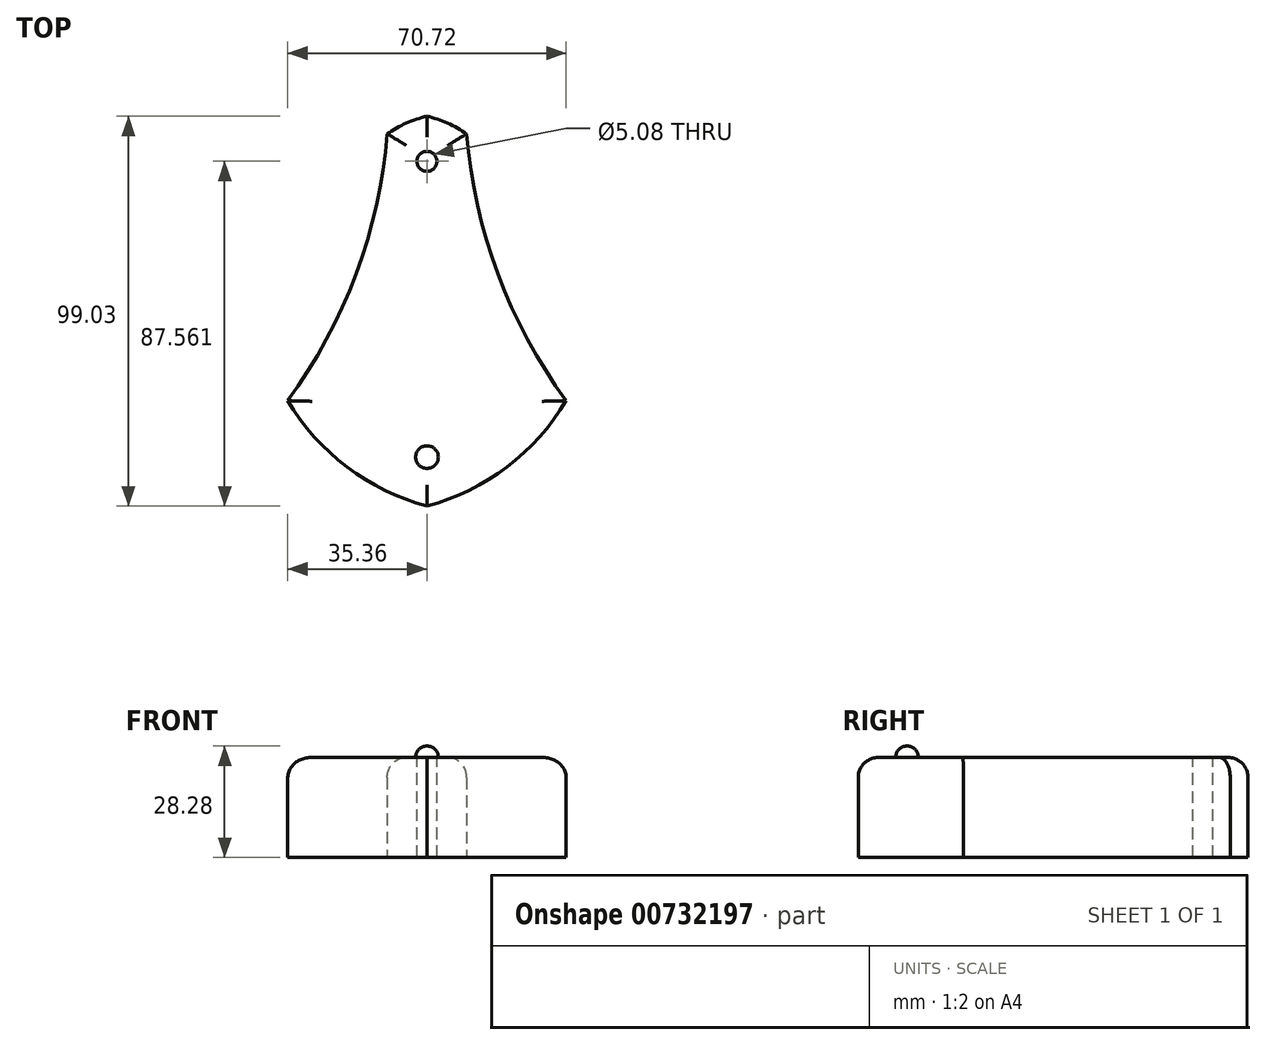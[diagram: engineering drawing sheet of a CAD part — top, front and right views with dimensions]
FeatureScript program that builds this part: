
annotation { "Feature Type Name" : "Feature", "Feature Type Description" : "" }
export const myFeature = defineFeature(function(context is Context, id is Id, definition is map)
    precondition{}
    {
        {
            var Q0;
            Q0=qCreatedBy(makeId("Top.planeOp"),FACE);
            var sketch = newSketch(context, id + "F0", { "sketchPlane" : qUnion([Q0])});
            skArc(sketch, "E0", {"start": v(0, 52.74) * mm, "mid": v(-5.26, 50.96) * mm, "end": v(-10.1, 48.22) * mm});
            skArc(sketch, "E1", {"start": v(-35.36, -19.52) * mm, "mid": v(-18.04, 12.6) * mm, "end": v(-10.1, 48.22) * mm});
            skArc(sketch, "E2", {"start": v(-35.36, -19.52) * mm, "mid": v(-20.32, -36.4) * mm, "end": v(0, -46.29) * mm});
            skArc(sketch, "E3.MirrorCS", {"start": v(35.36, -19.52) * mm, "mid": v(18.04, 12.6) * mm, "end": v(10.1, 48.22) * mm});
            skArc(sketch, "E4.MirrorCS", {"start": v(35.36, -19.52) * mm, "mid": v(20.32, -36.4) * mm, "end": v(0, -46.29) * mm});
            skArc(sketch, "E5.MirrorCS", {"start": v(0, 52.74) * mm, "mid": v(5.26, 50.96) * mm, "end": v(10.1, 48.22) * mm});
            skSolve(sketch);
        }
        {
            var Q0;
            Q0=makeQuery(id+"F0.imprint","IMPRINT",FACE,{"disambiguationData":[TD([[makeQuery(id+"F0.imprint","IMPRINT",EDGE,{"derivedFrom":sQuery(id+"F0.wireOp",EDGE,"E0")}),1.0]])]});
            extrude(context, id + "F1", {"entities" : qUnion([Q0]), "depth" : 25.4 * mm, "offsetDistance" : 25.4 * mm});
        }
        {
            var Q0;
            Q0=makeQuery(id+"F1.opExtrude","CAP_EDGE",EDGE,{"disambiguationData":[OSD([sQuery(id+"F0.wireOp",EDGE,"E2")])],"isStart":false});
            var Q1;
            Q1=makeQuery(id+"F1.opExtrude","CAP_FACE",FACE,{"disambiguationData":[OSD([sQuery(id+"F0.wireOp",EDGE,"E0"),sQuery(id+"F0.wireOp",EDGE,"E1"),sQuery(id+"F0.wireOp",EDGE,"E2"),sQuery(id+"F0.wireOp",EDGE,"E3.MirrorCS"),sQuery(id+"F0.wireOp",EDGE,"E4.MirrorCS"),sQuery(id+"F0.wireOp",EDGE,"E5.MirrorCS")])],"isStart":false});
            fillet(context, id + "F2", {"entities" : qUnion([Q0, Q1]), "radius" : 5.08 * mm, "tangentPropagation" : true, "allowEdgeOverflow" : false});
        }
        {
            var Q0;
            Q0=makeQuery(id+"F1.opExtrude","CAP_FACE",FACE,{"disambiguationData":[OSD([sQuery(id+"F0.wireOp",EDGE,"E0"),sQuery(id+"F0.wireOp",EDGE,"E1"),sQuery(id+"F0.wireOp",EDGE,"E2"),sQuery(id+"F0.wireOp",EDGE,"E3.MirrorCS"),sQuery(id+"F0.wireOp",EDGE,"E4.MirrorCS"),sQuery(id+"F0.wireOp",EDGE,"E5.MirrorCS")])],"isStart":false});
            var sketch = newSketch(context, id + "F3", { "sketchPlane" : qUnion([Q0])});
            skCircle(sketch, "E6", {"center": v(0, 41.27) * mm, "radius": 2.68 * mm});
            skSolve(sketch);
        }
        {
            var Q0;
            Q0=makeQuery(id+"F3.imprint","IMPRINT",FACE,{"disambiguationData":[TD([[makeQuery(id+"F3.imprint","IMPRINT",EDGE,{"derivedFrom":sQuery(id+"F3.wireOp",EDGE,"E6")}),-1.0]])]});
            var sketch = newSketch(context, id + "F4", { "sketchPlane" : qUnion([Q0])});
            skArc(sketch, "E7", {"start": v(0, -36.76) * mm, "mid": v(2.88, -33.88) * mm, "end": v(0, -31) * mm});
            skLineSegment(sketch, "E8", {"start": v(0, -31) * mm, "end": v(0, -36.76) * mm});
            skSolve(sketch);
        }
        {
            var Q0;
            Q0 = qSketchRegion(id + "F4", true);
            var Q1;
            Q1=sQuery(id+"F4.wireOp",EDGE,"E8");
            revolve(context, id + "F5", {"operationType" : NewBodyOperationType.ADD, "surfaceOperationType" : NewSurfaceOperationType.NEW, "entities" : qUnion([Q0]), "axis" : qUnion([Q1]), "revolveType" : RevolveType.FULL});
        }
        {
            var Q0;
            Q0=sQuery(id+"F3.wireOp",VERTEX,"E6.center");
            var Q1;
            Q1=makeQuery(id+"F1.opExtrude","SWEPT_BODY",BODY,{"disambiguationData":[OSD([sQuery(id+"F0.wireOp",EDGE,"E0"),sQuery(id+"F0.wireOp",EDGE,"E1"),sQuery(id+"F0.wireOp",EDGE,"E2"),sQuery(id+"F0.wireOp",EDGE,"E3.MirrorCS"),sQuery(id+"F0.wireOp",EDGE,"E4.MirrorCS"),sQuery(id+"F0.wireOp",EDGE,"E5.MirrorCS")])]});
            hole(context, id + "F6", {"style" : HoleStyle.SIMPLE, "endStyle" : HoleEndStyle.THROUGH, "holeDiameter" : 5.08 * mm, "majorDiameter" : 6.35 * mm, "isTappedThrough" : true, "tappedDepth" : 12.7 * mm, "tapClearance" : 3, "locations" : qUnion([Q0]), "scope" : qUnion([Q1])});
        }
    });
